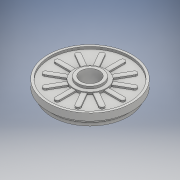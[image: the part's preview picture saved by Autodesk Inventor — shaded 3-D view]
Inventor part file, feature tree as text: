
AUTODESK INVENTOR PART (.ipt)
format: ipt  version: 2017 (Build 210142000, 142)  size: 273,920 bytes
history: native  units: mm
features: sketch x3, extrude x2, revolve x1
ambient origin geometry x8: Origin, YZ Plane, XZ Plane, XY Plane, X Axis, Y Axis, Z Axis, Center Point
bodies: Solid1 (feature_tree)
feature tree (6):
  revolve  "Revolution1"  [1 undecoded]
  extrude  "Extrusion1"  Depth=2.5mm
  extrude  "Extrusion2"  Depth=2.5mm
  sketch  "Sketch1"  dims[d0=27.0mm d1=3.0mm]
  sketch  "Sketch2"  dims[d2=4.5mm d3=2.5mm]
  sketch  "Sketch3"  dims[d4=2.0mm d5=2.5mm d6=4.0mm d7=2.0mm d8=1.5mm d9=8.0mm d10=3.0mm d11=2.0mm d12=1.5mm d13=1.0mm d14=1.5mm d15=1.5mm d16=5.0mm d17=90.0deg d18=13.0mm d19=1.0mm d20=3.0mm d21=1.5mm d22=1.5mm d23=120.0mm d25=360.0deg d27=1.0mm d28=0.0mm d29=2.0mm d30=2.5mm d31=1.0mm d32=0.0mm]
note: 1 required parameter value undecoded (feature->parameter linkage not recoverable at this tier; creation-order binding heuristic only, values carry confidence <= 0.55)
